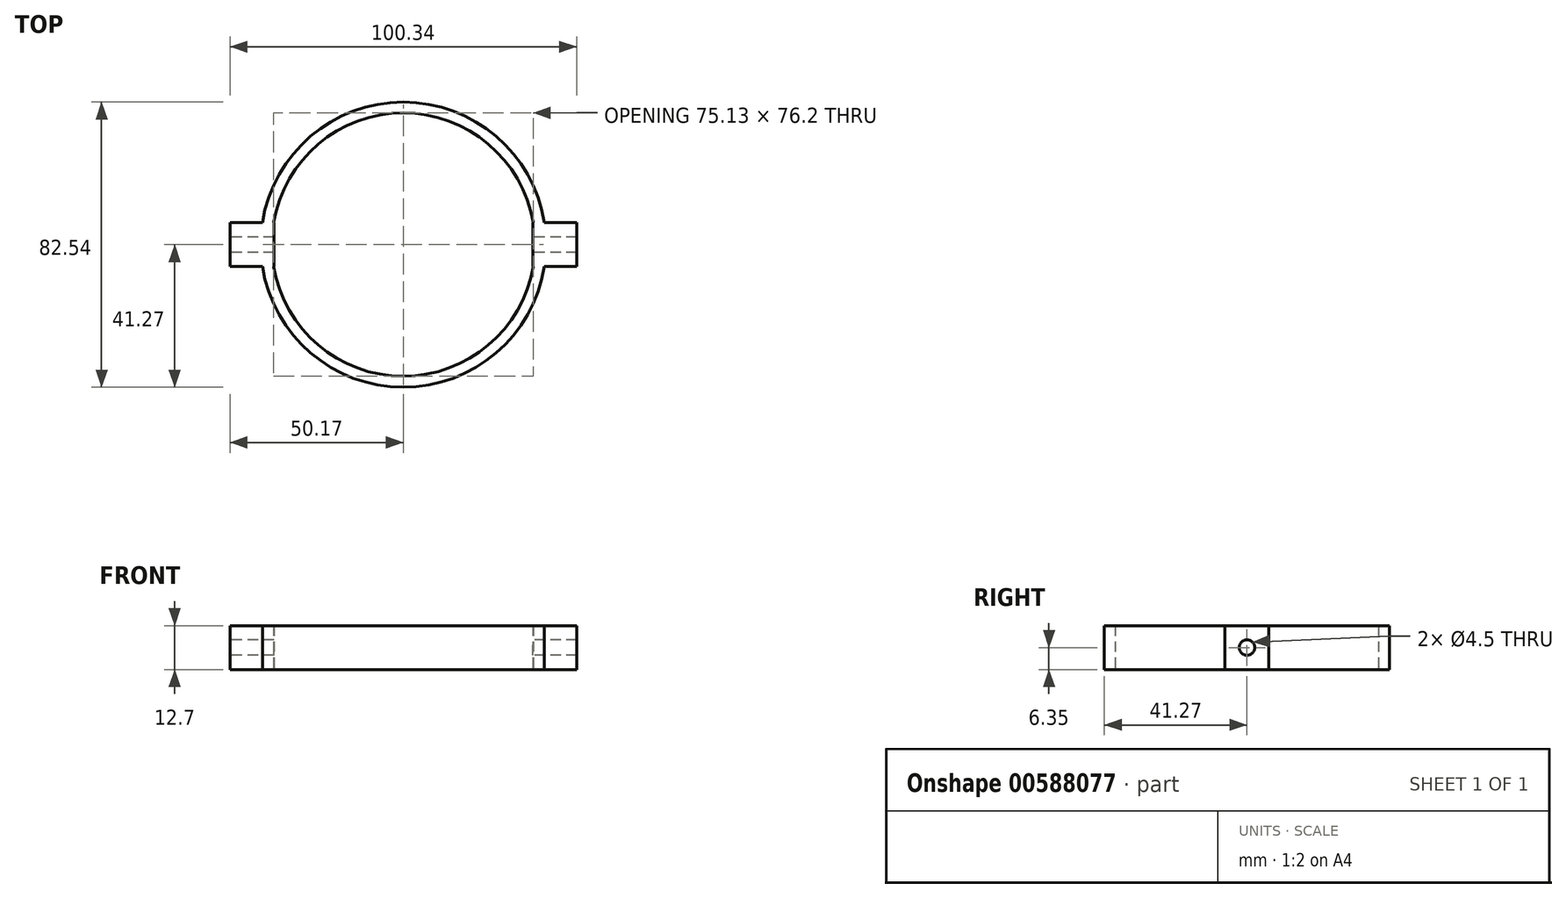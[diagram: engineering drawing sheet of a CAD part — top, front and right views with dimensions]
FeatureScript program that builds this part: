
annotation { "Feature Type Name" : "Feature", "Feature Type Description" : "" }
export const myFeature = defineFeature(function(context is Context, id is Id, definition is map)
    precondition{}
    {
        {
            var Q0;
            Q0=qCreatedBy(makeId("Top.planeOp"),FACE);
            var sketch = newSketch(context, id + "F0", { "sketchPlane" : qUnion([Q0])});
            skCircle(sketch, "E0", {"center": v(0, 0) * mm, "radius": 38.1 * mm});
            skCircle(sketch, "E1", {"center": v(0, 0) * mm, "radius": 41.28 * mm});
            skSolve(sketch);
        }
        {
            var Q0;
            Q0=makeQuery(id+"F0.imprint","IMPRINT",FACE,{"disambiguationData":[TD([[makeQuery(id+"F0.imprint","IMPRINT",EDGE,{"derivedFrom":sQuery(id+"F0.wireOp",EDGE,"E0")}),-1.0]])]});
            extrude(context, id + "F1", {"entities" : qUnion([Q0]), "depth" : 12.7 * mm, "offsetDistance" : 25.4 * mm});
        }
        {
            var Q0;
            Q0=qCreatedBy(makeId("Right.planeOp"),FACE);
            cPlane(context, id + "F2", {"entities" : qUnion([Q0]), "cplaneType" : CPlaneType.OFFSET, "offset" : 37.47 * mm, "width" : 152.4 * mm, "height" : 152.4 * mm});
        }
        {
            var Q0;
            Q0=qCreatedBy(id+"F2.planeOp",FACE);
            var sketch = newSketch(context, id + "F3", { "sketchPlane" : qUnion([Q0])});
            skLineSegment(sketch, "E2.bottom", {"start": v(-6.35, 12.7) * mm, "end": v(6.35, 12.7) * mm});
            skLineSegment(sketch, "E2.top", {"start": v(-6.35, 0) * mm, "end": v(6.35, 0) * mm});
            skLineSegment(sketch, "E2.left", {"start": v(-6.35, 12.7) * mm, "end": v(-6.35, 0) * mm});
            skLineSegment(sketch, "E2.right", {"start": v(6.35, 12.7) * mm, "end": v(6.35, 0) * mm});
            skSolve(sketch);
        }
        {
            var Q0;
            Q0 = qSketchRegion(id + "F3", true);
            var Q1;
            Q1=sQuery(id+"F3.wireOp",EDGE,"E2.left");
            var Q2;
            Q2=sQuery(id+"F3.wireOp",EDGE,"E2.bottom");
            var Q3;
            Q3=sQuery(id+"F3.wireOp",EDGE,"E2.right");
            var Q4;
            Q4=sQuery(id+"F3.wireOp",EDGE,"E2.top");
            extrude(context, id + "F4", {"entities" : qUnion([Q0]), "operationType" : NewBodyOperationType.ADD, "surfaceEntities" : qUnion([Q1, Q2, Q3, Q4]), "depth" : 12.7 * mm, "offsetDistance" : 25.4 * mm});
        }
        {
            var Q0;
            Q0=qCreatedBy(makeId("Right.planeOp"),FACE);
            cPlane(context, id + "F5", {"entities" : qUnion([Q0]), "cplaneType" : CPlaneType.OFFSET, "offset" : 37.47 * mm, "oppositeDirection" : true, "width" : 152.4 * mm, "height" : 152.4 * mm});
        }
        {
            var Q0;
            Q0=qCreatedBy(id+"F5.planeOp",FACE);
            var sketch = newSketch(context, id + "F6", { "sketchPlane" : qUnion([Q0])});
            skLineSegment(sketch, "E3.bottom", {"start": v(-6.35, 12.7) * mm, "end": v(6.35, 12.7) * mm});
            skLineSegment(sketch, "E3.top", {"start": v(-6.35, 0) * mm, "end": v(6.35, 0) * mm});
            skLineSegment(sketch, "E3.left", {"start": v(-6.35, 12.7) * mm, "end": v(-6.35, 0) * mm});
            skLineSegment(sketch, "E3.right", {"start": v(6.35, 12.7) * mm, "end": v(6.35, 0) * mm});
            skPoint(sketch, "E4.endSnap0", {"position": v(-6.35, 6.35) * mm});
            skSolve(sketch);
        }
        {
            var Q0;
            Q0 = qSketchRegion(id + "F6", true);
            extrude(context, id + "F7", {"entities" : qUnion([Q0]), "operationType" : NewBodyOperationType.ADD, "oppositeDirection" : true, "depth" : 12.7 * mm, "offsetDistance" : 25.4 * mm});
        }
        {
            var Q0;
            Q0=makeQuery(id+"F7.opExtrude","CAP_FACE",FACE,{"disambiguationData":[OSD([sQuery(id+"F6.wireOp",EDGE,"E3.bottom"),sQuery(id+"F6.wireOp",EDGE,"E3.top"),sQuery(id+"F6.wireOp",EDGE,"E3.left"),sQuery(id+"F6.wireOp",EDGE,"E3.right")])],"isStart":false});
            var sketch = newSketch(context, id + "F8", { "sketchPlane" : qUnion([Q0])});
            skLineSegment(sketch, "E5", {"start": v(0, 0) * mm, "end": v(0, 6.35) * mm});
            skPoint(sketch, "E5.endSnap0", {"position": v(6.35, 6.35) * mm});
            skSolve(sketch);
        }
        {
            var Q0;
            Q0=sQuery(id+"F8.wireOp",VERTEX,"E5.end");
            var Q1;
            Q1=makeQuery(id+"F1.opExtrude","SWEPT_BODY",BODY,{"disambiguationData":[OSD([sQuery(id+"F0.wireOp",EDGE,"E0"),sQuery(id+"F0.wireOp",EDGE,"E1")])]});
            hole(context, id + "F9", {"style" : HoleStyle.SIMPLE, "endStyle" : HoleEndStyle.THROUGH, "standardTappedOrClearance" : lookupTablePath({ "standard" : "ANSI", "fit" : "Normal (ASME)", "size" : "#8", "type" : "Clearance" }), "standardBlindInLast" : lookupTablePath({ "fit" : "Free", "standard" : "ANSI", "size" : "#8", "type" : "Clearance" }), "holeDiameter" : 4.5 * mm, "majorDiameter" : 6.35 * mm, "isTappedThrough" : true, "tappedDepth" : 22.22 * mm, "tapClearance" : 3, "locations" : qUnion([Q0]), "scope" : qUnion([Q1])});
        }
    });
